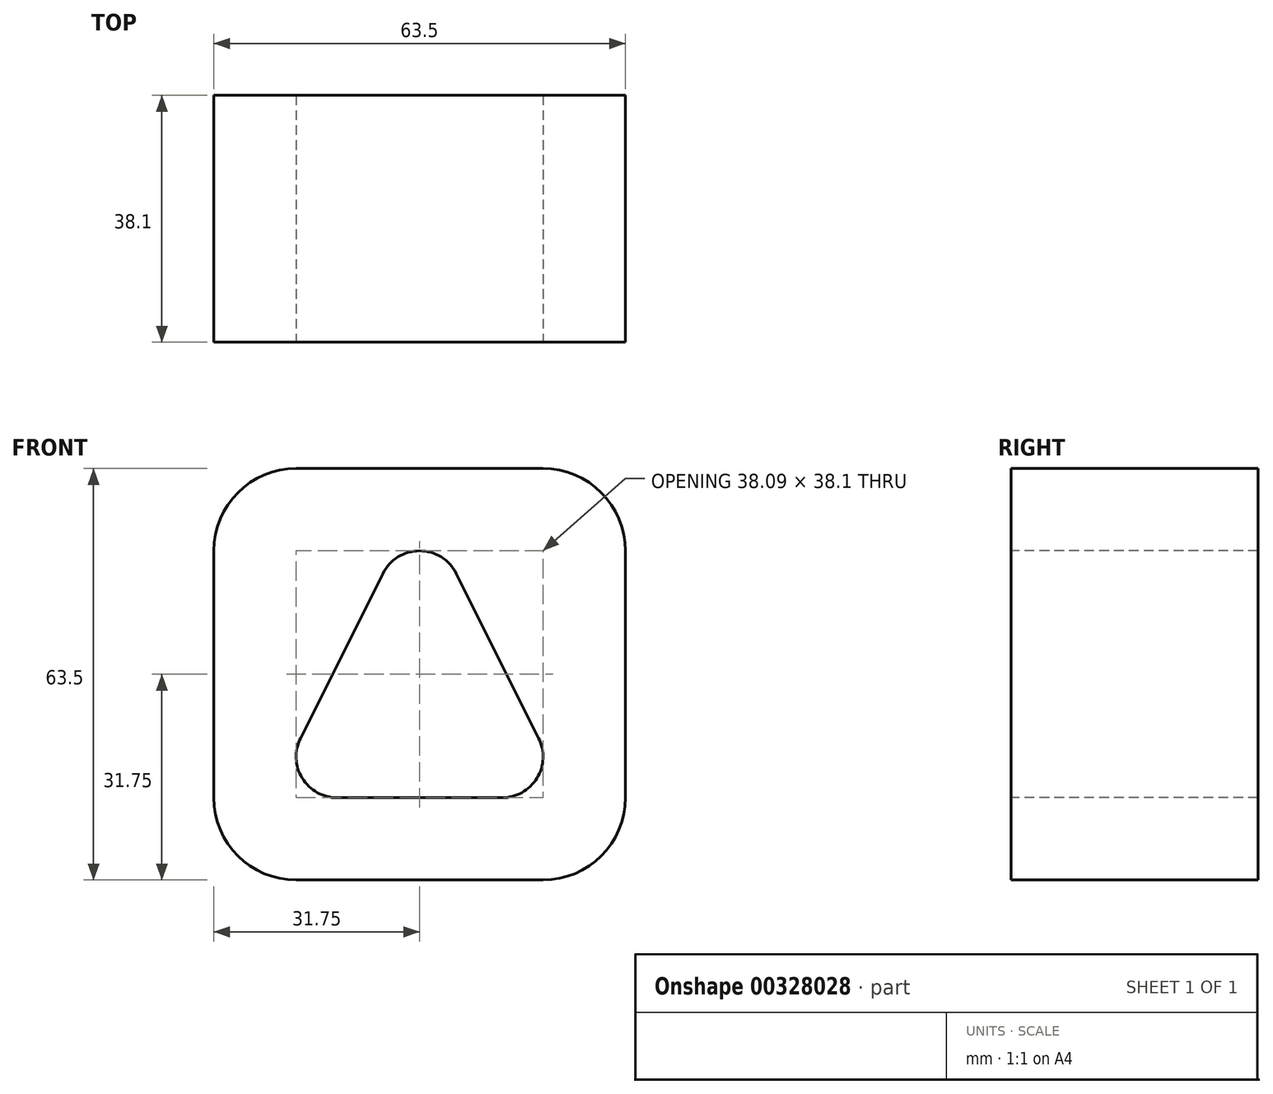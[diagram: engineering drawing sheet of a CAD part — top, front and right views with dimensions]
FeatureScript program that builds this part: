
annotation { "Feature Type Name" : "Feature", "Feature Type Description" : "" }
export const myFeature = defineFeature(function(context is Context, id is Id, definition is map)
    precondition{}
    {
        {
            var Q0;
            Q0=qCreatedBy(makeId("Front.planeOp"),FACE);
            var sketch = newSketch(context, id + "F0", { "sketchPlane" : qUnion([Q0])});
            skLineSegment(sketch, "E0.bottom", {"start": v(0, 0) * mm, "end": v(63.5, 0) * mm});
            skLineSegment(sketch, "E0.top", {"start": v(0, 63.5) * mm, "end": v(63.5, 63.5) * mm});
            skLineSegment(sketch, "E0.left", {"start": v(0, 0) * mm, "end": v(0, 63.5) * mm});
            skLineSegment(sketch, "E0.right", {"start": v(63.5, 0) * mm, "end": v(63.5, 63.5) * mm});
            skArc(sketch, "E1", {"start": v(13.37, 21.89) * mm, "mid": v(13.65, 15.71) * mm, "end": v(19.05, 12.7) * mm});
            skArc(sketch, "E2", {"start": v(37.43, 47.29) * mm, "mid": v(31.75, 50.8) * mm, "end": v(26.07, 47.29) * mm});
            skArc(sketch, "E3", {"start": v(44.45, 12.7) * mm, "mid": v(49.85, 15.71) * mm, "end": v(50.13, 21.89) * mm});
            skLineSegment(sketch, "E4", {"start": v(37.43, 47.29) * mm, "end": v(50.13, 21.89) * mm});
            skLineSegment(sketch, "E5", {"start": v(26.07, 47.29) * mm, "end": v(13.37, 21.89) * mm});
            skLineSegment(sketch, "E6", {"start": v(19.05, 12.7) * mm, "end": v(44.45, 12.7) * mm});
            skSolve(sketch);
        }
        {
            var Q0;
            Q0=makeQuery(id+"F0.imprint","IMPRINT",FACE,{"disambiguationData":[TD([[makeQuery(id+"F0.imprint","IMPRINT",EDGE,{"derivedFrom":sQuery(id+"F0.wireOp",EDGE,"E0.bottom")}),1.0]])]});
            extrude(context, id + "F1", {"entities" : qUnion([Q0]), "oppositeDirection" : true, "depth" : 38.1 * mm});
        }
        {
            var Q0;
            Q0=makeQuery(id+"F1.opExtrude","SWEPT_EDGE",EDGE,{"disambiguationData":[OSD([sQuery(id+"F0.wireOp",EDGE,"E0.top"),sQuery(id+"F0.wireOp",EDGE,"E0.right")])]});
            var Q1;
            Q1=makeQuery(id+"F1.opExtrude","SWEPT_EDGE",EDGE,{"disambiguationData":[OSD([sQuery(id+"F0.wireOp",EDGE,"E0.bottom"),sQuery(id+"F0.wireOp",EDGE,"E0.right")])]});
            var Q2;
            Q2=makeQuery(id+"F1.opExtrude","SWEPT_EDGE",EDGE,{"disambiguationData":[OSD([sQuery(id+"F0.wireOp",EDGE,"E0.top"),sQuery(id+"F0.wireOp",EDGE,"E0.left")])]});
            var Q3;
            Q3=makeQuery(id+"F1.opExtrude","SWEPT_EDGE",EDGE,{"disambiguationData":[OSD([sQuery(id+"F0.wireOp",EDGE,"E0.bottom"),sQuery(id+"F0.wireOp",EDGE,"E0.left")])]});
            fillet(context, id + "F2", {"entities" : qUnion([Q0, Q1, Q2, Q3]), "radius" : 12.7 * mm, "tangentPropagation" : true, "allowEdgeOverflow" : false});
        }
    });
